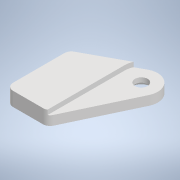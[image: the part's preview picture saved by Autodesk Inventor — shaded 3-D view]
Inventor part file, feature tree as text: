
AUTODESK INVENTOR PART (.ipt)
format: ipt  version: 2022 (Build 260153000, 153)  size: 161,792 bytes
history: native  units: mm
features: other x5, reference x3, extrude x2, sketch x2, chamfer x1, fillet x1, projected_geometry x1
ambient origin geometry x8: Origin, YZ Plane, XZ Plane, XY Plane, X Axis, Y Axis, Z Axis, Center Point
bodies: Body1 (feature_tree)
feature tree (15):
  other  "Твердое тело1"
  extrude  "Выдавливание1"  Depth=2.7mm
  chamfer  "Фаска1"  Distance=0.3mm
  fillet  "Сопряжение1"  Radius=7.0mm
  extrude  "Выдавливание2"  Depth=4.5mm
  sketch  "Эскиз1"
  reference  "Ссылка1"
  reference  "Ссылка2"
  sketch  "Эскиз2"
  reference  "Ссылка3"
  projected_geometry  "Спроецированная петля1"
  other  "<userpath>\Documents\Git\MZCAT_2024_construction\MZCAT_2024_RPI_2\MZCAT_4.iam"
  other  "MZCAT_4.iam"
  other  "MZCAT_motherboard_fnl:1"
  other  "30mm Fan Mockup 3010 v5:1"
